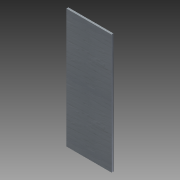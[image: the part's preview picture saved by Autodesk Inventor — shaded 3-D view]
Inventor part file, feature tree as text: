
AUTODESK INVENTOR PART (.ipt)
format: ipt  version: 2011 SP1 (Build 150282100, 282)  size: 81,408 bytes
history: native  units: in
note: dims shown in document units (in); Inventor stores cm internally (conversion verified against a paired STEP export)
features: extrude x1, hole x1, sketch x1
ambient origin geometry x8: Origin, YZ Plane, XZ Plane, XY Plane, X Axis, Y Axis, Z Axis, Center Point
bodies: Solid1 (feature_tree)
feature tree (3):
  extrude  "Extrusion1"  Depth=3.0in
  hole  "Hole1"  [1 undecoded]
  sketch  "Sketch1"  dims[d0=7.75in d1=3.0in d2=0.125in d3=0.0in d4=0.0625in d5=3.0in d6=0.187in d7=0.75in d8=0.375in d9=0.25in d10=0.5635in d11=9.0in d12=0.8108in]
note: 1 required parameter value undecoded (feature->parameter linkage not recoverable at this tier; creation-order binding heuristic only, values carry confidence <= 0.55)
